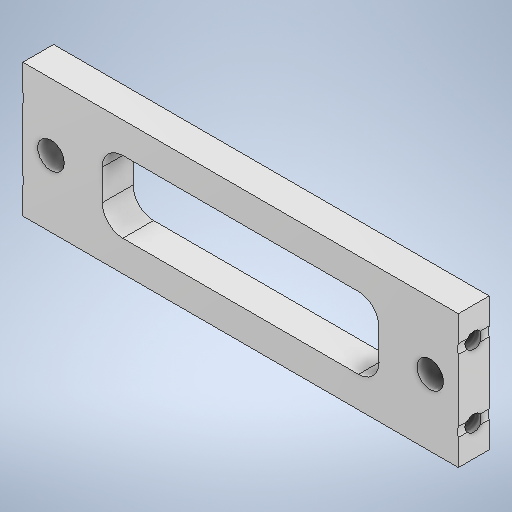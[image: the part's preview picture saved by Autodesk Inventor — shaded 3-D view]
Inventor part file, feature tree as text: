
AUTODESK INVENTOR PART (.ipt)
format: ipt  version: 2025.1 (Build 291241000, 241)  size: 308,736 bytes
history: native  units: mm
features: sketch x5, extrude x3, hole x2, other x1, fillet x1
ambient origin geometry x8: Origin, YZ Plane, XZ Plane, XY Plane, X Axis, Y Axis, Z Axis, Center Point
bodies: Body1 (feature_tree)
feature tree (12):
  other  "ソリッド1"
  extrude  "押し出し1"  Depth=2.6mm
  extrude  "押し出し2"  Depth=2.6mm
  fillet  "フィレット3"  Radius=37.0mm
  hole  "穴1"  [1 undecoded]
  hole  "穴2"  [1 undecoded]
  extrude  "押し出し8"  Depth=3.0mm TaperAngle=0.0deg
  sketch  "スケッチ1"
  sketch  "スケッチ2"
  sketch  "スケッチ9"
  sketch  "スケッチ10"
  sketch  "スケッチ11"
note: 2 required parameter values undecoded (feature->parameter linkage not recoverable at this tier; creation-order binding heuristic only, values carry confidence <= 0.55)
